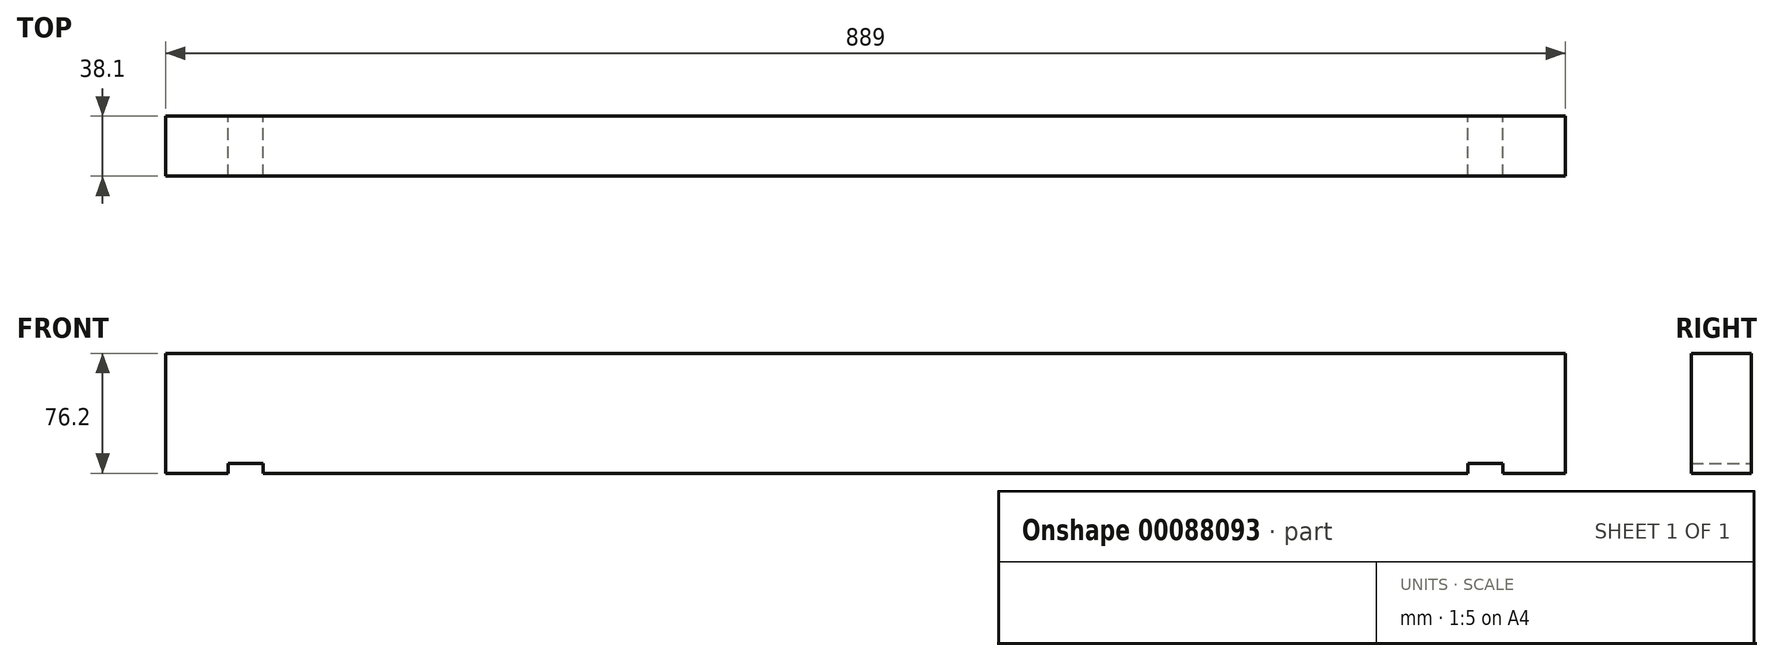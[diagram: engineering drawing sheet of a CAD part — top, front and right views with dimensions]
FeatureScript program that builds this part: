
annotation { "Feature Type Name" : "Feature", "Feature Type Description" : "" }
export const myFeature = defineFeature(function(context is Context, id is Id, definition is map)
    precondition{}
    {
        {
            var Q0;
            Q0=qCreatedBy(makeId("Right.planeOp"),FACE);
            var sketch = newSketch(context, id + "F0", { "sketchPlane" : qUnion([Q0])});
            skLineSegment(sketch, "E0.bottom", {"start": v(-19.05, 38.1) * mm, "end": v(19.05, 38.1) * mm});
            skLineSegment(sketch, "E0.top", {"start": v(-19.05, -38.1) * mm, "end": v(19.05, -38.1) * mm});
            skLineSegment(sketch, "E0.left", {"start": v(-19.05, 38.1) * mm, "end": v(-19.05, -38.1) * mm});
            skLineSegment(sketch, "E0.right", {"start": v(19.05, 38.1) * mm, "end": v(19.05, -38.1) * mm});
            skSolve(sketch);
        }
        {
            var Q0;
            Q0=makeQuery(id+"F0.imprint","IMPRINT",FACE,{"disambiguationData":[TD([[makeQuery(id+"F0.imprint","IMPRINT",EDGE,{"derivedFrom":sQuery(id+"F0.wireOp",EDGE,"E0.bottom")}),-1.0]])]});
            extrude(context, id + "F1", {"entities" : qUnion([Q0]), "endBound" : BoundingType.SYMMETRIC, "depth" : 889 * mm});
        }
        {
            var Q0;
            Q0=makeQuery(id+"F1.opExtrude","SWEPT_FACE",FACE,{"disambiguationData":[OSD([sQuery(id+"F0.wireOp",EDGE,"E0.top")])]});
            var sketch = newSketch(context, id + "F2", { "sketchPlane" : qUnion([Q0])});
            skLineSegment(sketch, "E1.0.0", {"start": v(-444.5, 19.05) * mm, "end": v(-444.5, -19.05) * mm});
            skLineSegment(sketch, "E1.0.1", {"start": v(-444.5, -19.05) * mm, "end": v(444.5, -19.05) * mm});
            skLineSegment(sketch, "E1.0.2", {"start": v(444.5, -19.05) * mm, "end": v(444.5, 19.05) * mm});
            skLineSegment(sketch, "E1.0.3", {"start": v(444.5, 19.05) * mm, "end": v(-444.5, 19.05) * mm});
            skLineSegment(sketch, "E2", {"start": v(404.7, 19.05) * mm, "end": v(404.7, -19.05) * mm});
            skLineSegment(sketch, "E3", {"start": v(382.7, 19.05) * mm, "end": v(382.7, -19.05) * mm});
            skCircle(sketch, "E4", {"center": v(313.59, -94.37) * mm, "radius": 12.7 * mm, "construction": true});
            skLineSegment(sketch, "E5", {"start": v(295.1, -107.07) * mm, "end": v(335.4, -107.07) * mm, "construction": true});
            skLineSegment(sketch, "E6", {"start": v(324.59, -107.07) * mm, "end": v(324.59, -100.72) * mm, "construction": true});
            skLineSegment(sketch, "E7", {"start": v(302.59, -107.07) * mm, "end": v(302.59, -100.72) * mm, "construction": true});
            skLineSegment(sketch, "E8", {"start": v(393.7, 19.05) * mm, "end": v(393.7, -19.05) * mm, "construction": true});
            skLineSegment(sketch, "E9", {"start": v(0, 19.05) * mm, "end": v(0, -19.05) * mm, "construction": true});
            skLineSegment(sketch, "E10.MirrorCS", {"start": v(-382.7, 19.05) * mm, "end": v(-382.7, -19.05) * mm});
            skLineSegment(sketch, "E11.MirrorCS", {"start": v(-404.7, 19.05) * mm, "end": v(-404.7, -19.05) * mm});
            skLineSegment(sketch, "E12.MirrorCS", {"start": v(-393.7, 19.05) * mm, "end": v(-393.7, -19.05) * mm, "construction": true});
            skSolve(sketch);
        }
        {
            var Q0;
            {var subQ0=sQuery(id+"F2.wireOp",EDGE,"E2");Q0=makeQuery(id+"F2.imprint","IMPRINT",FACE,{"disambiguationData":[TD([[makeQuery(id+"F2.imprint","IMPRINT",EDGE,{"derivedFrom":subQ0}),-1.0]])]});}
            var Q1;
            {var subQ0=sQuery(id+"F2.wireOp",EDGE,"E10.MirrorCS");Q1=makeQuery(id+"F2.imprint","IMPRINT",FACE,{"disambiguationData":[TD([[makeQuery(id+"F2.imprint","IMPRINT",EDGE,{"derivedFrom":subQ0}),-1.0]])]});}
            extrude(context, id + "F3", {"entities" : qUnion([Q0, Q1]), "operationType" : NewBodyOperationType.REMOVE, "oppositeDirection" : true, "depth" : 6.35 * mm});
        }
    });
